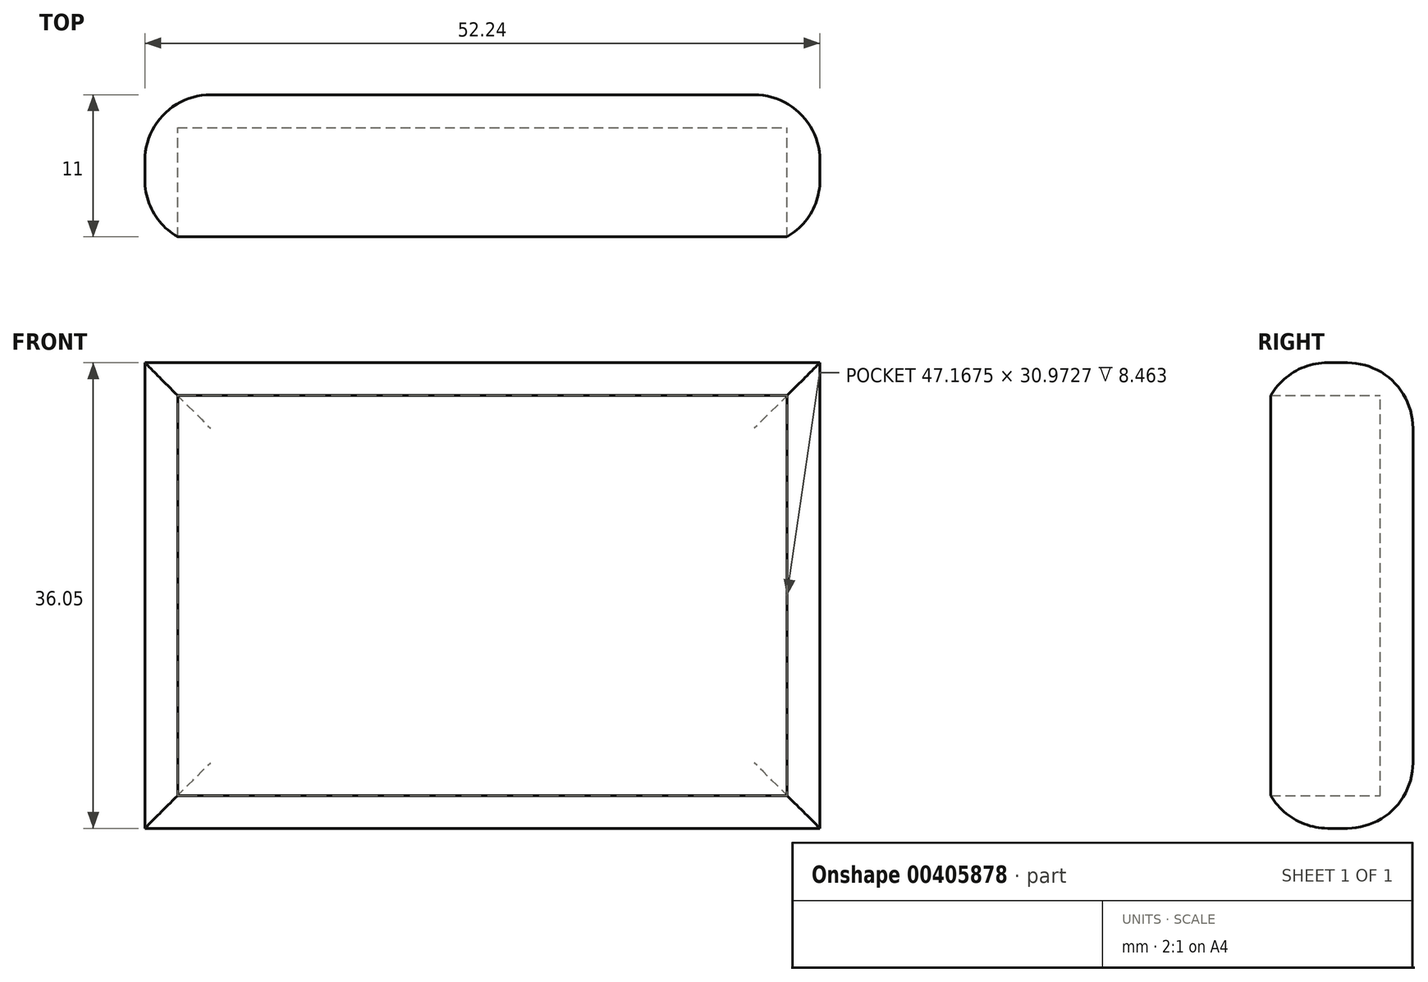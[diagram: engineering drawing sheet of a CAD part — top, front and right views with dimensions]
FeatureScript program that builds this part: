
annotation { "Feature Type Name" : "Feature", "Feature Type Description" : "" }
export const myFeature = defineFeature(function(context is Context, id is Id, definition is map)
    precondition{}
    {
        {
            var Q0;
            Q0=qCreatedBy(makeId("Front.planeOp"),FACE);
            var sketch = newSketch(context, id + "F0", { "sketchPlane" : qUnion([Q0])});
            skLineSegment(sketch, "E0.bottom", {"start": v(-31.23, 0) * mm, "end": v(21.01, 0) * mm});
            skLineSegment(sketch, "E0.top", {"start": v(-31.23, 36.05) * mm, "end": v(21.01, 36.05) * mm});
            skLineSegment(sketch, "E0.left", {"start": v(-31.23, 0) * mm, "end": v(-31.23, 36.05) * mm});
            skLineSegment(sketch, "E0.right", {"start": v(21.01, 0) * mm, "end": v(21.01, 36.05) * mm});
            skSolve(sketch);
        }
        {
            var Q0;
            Q0=makeQuery(id+"F0.imprint","IMPRINT",FACE,{"disambiguationData":[TD([[makeQuery(id+"F0.imprint","IMPRINT",EDGE,{"derivedFrom":sQuery(id+"F0.wireOp",EDGE,"E0.bottom")}),1.0]])]});
            extrude(context, id + "F1", {"entities" : qUnion([Q0]), "depth" : 11.68 * mm});
        }
        {
            var Q0;
            Q0=makeQuery(id+"F1.opExtrude","CAP_FACE",FACE,{"disambiguationData":[OSD([sQuery(id+"F0.wireOp",EDGE,"E0.bottom"),sQuery(id+"F0.wireOp",EDGE,"E0.top"),sQuery(id+"F0.wireOp",EDGE,"E0.left"),sQuery(id+"F0.wireOp",EDGE,"E0.right")])],"isStart":false});
            shell(context, id + "F2", {"entities" : qUnion([Q0]), "thickness" : 2.54 * mm});
        }
        {
            var Q0;
            Q0=makeQuery(id+"F1.opExtrude","CAP_EDGE",EDGE,{"disambiguationData":[OSD([sQuery(id+"F0.wireOp",EDGE,"E0.right")])],"isStart":false});
            var Q1;
            Q1=makeQuery(id+"F1.opExtrude","CAP_EDGE",EDGE,{"disambiguationData":[OSD([sQuery(id+"F0.wireOp",EDGE,"E0.top")])],"isStart":false});
            var Q2;
            Q2=makeQuery(id+"F1.opExtrude","CAP_EDGE",EDGE,{"disambiguationData":[OSD([sQuery(id+"F0.wireOp",EDGE,"E0.bottom")])],"isStart":false});
            var Q3;
            Q3=makeQuery(id+"F1.opExtrude","CAP_EDGE",EDGE,{"disambiguationData":[OSD([sQuery(id+"F0.wireOp",EDGE,"E0.left")])],"isStart":false});
            fillet(context, id + "F3", {"entities" : qUnion([Q0, Q1, Q2, Q3]), "radius" : 5.08 * mm, "tangentPropagation" : true, "allowEdgeOverflow" : false});
        }
        {
            var Q0;
            Q0=makeQuery(id+"F1.opExtrude","CAP_EDGE",EDGE,{"disambiguationData":[OSD([sQuery(id+"F0.wireOp",EDGE,"E0.bottom")])],"isStart":true});
            var Q1;
            Q1=makeQuery(id+"F1.opExtrude","CAP_EDGE",EDGE,{"disambiguationData":[OSD([sQuery(id+"F0.wireOp",EDGE,"E0.left")])],"isStart":true});
            var Q2;
            Q2=makeQuery(id+"F1.opExtrude","CAP_EDGE",EDGE,{"disambiguationData":[OSD([sQuery(id+"F0.wireOp",EDGE,"E0.top")])],"isStart":true});
            var Q3;
            Q3=makeQuery(id+"F1.opExtrude","CAP_EDGE",EDGE,{"disambiguationData":[OSD([sQuery(id+"F0.wireOp",EDGE,"E0.right")])],"isStart":true});
            fillet(context, id + "F4", {"entities" : qUnion([Q0, Q1, Q2, Q3]), "radius" : 5.08 * mm, "tangentPropagation" : true, "allowEdgeOverflow" : false});
        }
    });
